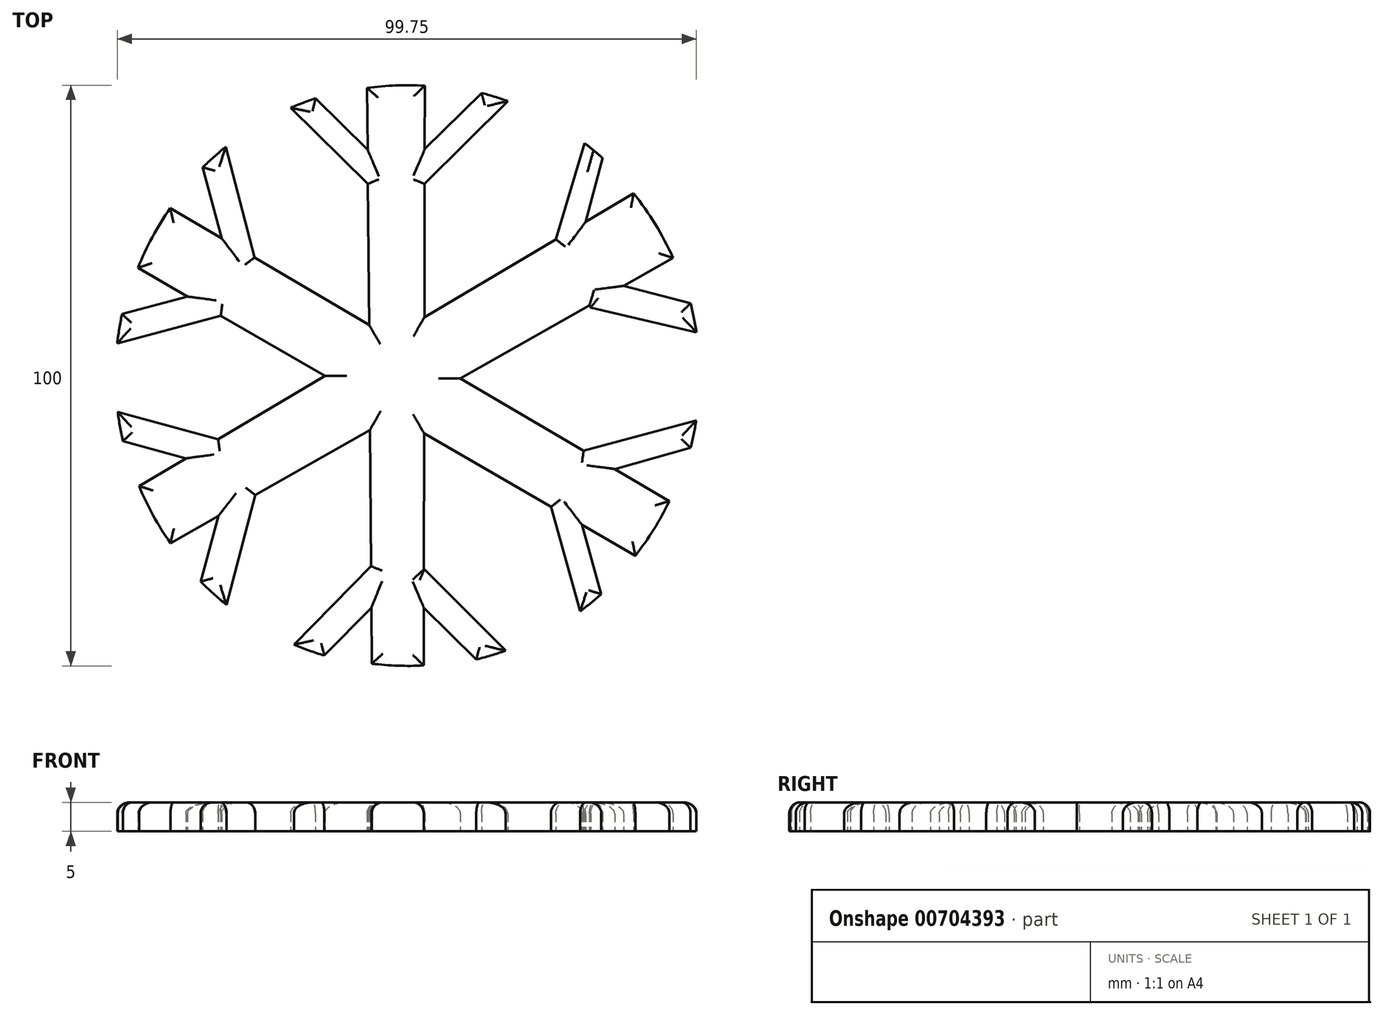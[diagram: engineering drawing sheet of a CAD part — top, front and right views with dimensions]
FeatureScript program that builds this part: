
annotation { "Feature Type Name" : "Feature", "Feature Type Description" : "" }
export const myFeature = defineFeature(function(context is Context, id is Id, definition is map)
    precondition{}
    {
        {
            var Q0;
            Q0=qCreatedBy(makeId("Top.planeOp"),FACE);
            var sketch = newSketch(context, id + "F0", { "sketchPlane" : qUnion([Q0])});
            skArc(sketch, "E0", {"start": v(-39.33, 28.82) * mm, "mid": v(-42.42, 23.84) * mm, "end": v(-44.9, 18.55) * mm});
            skPoint(sketch, "E1.center", {"position": v(0, 0) * mm});
            skLineSegment(sketch, "E2", {"start": v(-5.43, 49.51) * mm, "end": v(-4.63, -49.62) * mm});
            skLineSegment(sketch, "E3", {"start": v(-39.33, 28.82) * mm, "end": v(46.61, -21.62) * mm});
            skLineSegment(sketch, "E4", {"start": v(-44.7, -19.02) * mm, "end": v(40.46, 31.38) * mm});
            skLineSegment(sketch, "E5.MirrorCS", {"start": v(-39.3, -28.86) * mm, "end": v(47.24, 20.26) * mm});
            skLineSegment(sketch, "E6.MirrorCS", {"start": v(4.5, 49.91) * mm, "end": v(4.3, -49.92) * mm});
            skLineSegment(sketch, "E7.MirrorCS", {"start": v(-44.9, 18.55) * mm, "end": v(40.75, -31.02) * mm});
            skArc(sketch, "E8.trimOffspring", {"start": v(4.5, 49.91) * mm, "mid": v(-0.48, 49.96) * mm, "end": v(-5.43, 49.51) * mm});
            skArc(sketch, "E9.trimOffspring", {"start": v(-4.63, -49.62) * mm, "mid": v(-0.17, -49.97) * mm, "end": v(4.3, -49.92) * mm});
            skArc(sketch, "E10.trimOffspring", {"start": v(40.75, -31.02) * mm, "mid": v(43.94, -26.48) * mm, "end": v(46.61, -21.62) * mm});
            skArc(sketch, "E11.trimOffspring", {"start": v(47.24, 20.26) * mm, "mid": v(44.21, 26.04) * mm, "end": v(40.46, 31.38) * mm});
            skArc(sketch, "E12.trimOffspring", {"start": v(-44.7, -19.02) * mm, "mid": v(-42.28, -24.1) * mm, "end": v(-39.3, -28.86) * mm});
            skLineSegment(sketch, "E13", {"start": v(-24.84, 20.31) * mm, "end": v(-30.64, 10.3) * mm});
            skLineSegment(sketch, "E14", {"start": v(-24.84, 20.31) * mm, "end": v(-29.8, 39.35) * mm});
            skLineSegment(sketch, "E15", {"start": v(-30.64, 10.3) * mm, "end": v(-48.47, 5.54) * mm});
            skLineSegment(sketch, "E16", {"start": v(-48.47, 5.54) * mm, "end": v(-30.64, 10.3) * mm});
            skLineSegment(sketch, "E17", {"start": v(4.47, 33) * mm, "end": v(-5.3, 33) * mm});
            skLineSegment(sketch, "E18", {"start": v(4.47, 33) * mm, "end": v(18.77, 47.25) * mm});
            skLineSegment(sketch, "E19", {"start": v(-18.6, 46.1) * mm, "end": v(-5.3, 33) * mm});
            skArc(sketch, "E20", {"start": v(-29.8, 39.35) * mm, "mid": v(-31.82, 37.66) * mm, "end": v(-33.75, 35.86) * mm});
            skLineSegment(sketch, "E21.MirrorCS", {"start": v(-18.06, -46.33) * mm, "end": v(-4.77, -32.83) * mm});
            skLineSegment(sketch, "E22.MirrorCS", {"start": v(4.44, -33.37) * mm, "end": v(-4.77, -32.83) * mm});
            skLineSegment(sketch, "E23.MirrorCS", {"start": v(4.44, -33.37) * mm, "end": v(18.4, -47.39) * mm});
            skLineSegment(sketch, "E24.MirrorCS", {"start": v(31.78, -12.97) * mm, "end": v(51.24, -7.7) * mm});
            skLineSegment(sketch, "E25.MirrorCS", {"start": v(31.78, -12.97) * mm, "end": v(26.23, -22.61) * mm});
            skLineSegment(sketch, "E26.MirrorCS", {"start": v(31.24, -40.59) * mm, "end": v(26.23, -22.61) * mm});
            skLineSegment(sketch, "E27.MirrorCS", {"start": v(-24.7, -20.57) * mm, "end": v(-29.65, -39.47) * mm});
            skLineSegment(sketch, "E28.MirrorCS", {"start": v(-24.71, -20.64) * mm, "end": v(-30.29, -11) * mm});
            skLineSegment(sketch, "E29.MirrorCS", {"start": v(-48.38, -6.26) * mm, "end": v(-30.64, -11.09) * mm});
            skLineSegment(sketch, "E30.MirrorCS", {"start": v(33.06, 11.7) * mm, "end": v(27.08, 23.46) * mm});
            skLineSegment(sketch, "E31.MirrorCS", {"start": v(32, 40.02) * mm, "end": v(27.08, 23.46) * mm});
            skLineSegment(sketch, "E32.MirrorCS", {"start": v(33.06, 11.7) * mm, "end": v(51.28, 7.45) * mm});
            skLineSegment(sketch, "E33", {"start": v(-47.48, -11.31) * mm, "end": v(-36.66, -14.26) * mm});
            skLineSegment(sketch, "E34", {"start": v(-36.66, -14.26) * mm, "end": v(-31.04, -24.17) * mm});
            skLineSegment(sketch, "E35", {"start": v(-31.04, -24.17) * mm, "end": v(-34.12, -35.48) * mm});
            skLineSegment(sketch, "E36", {"start": v(-12.8, -48.22) * mm, "end": v(-4.71, -40) * mm});
            skLineSegment(sketch, "E37", {"start": v(-4.71, -40) * mm, "end": v(4.33, -40) * mm});
            skLineSegment(sketch, "E38", {"start": v(4.33, -40) * mm, "end": v(13.36, -48.89) * mm});
            skLineSegment(sketch, "E39", {"start": v(34.9, -37.64) * mm, "end": v(31.56, -25.7) * mm});
            skLineSegment(sketch, "E40", {"start": v(31.56, -25.7) * mm, "end": v(37.2, -16.1) * mm});
            skLineSegment(sketch, "E41", {"start": v(37.2, -16.1) * mm, "end": v(50.27, -12.44) * mm});
            skLineSegment(sketch, "E42", {"start": v(50.27, 12.44) * mm, "end": v(38.77, 15.45) * mm});
            skLineSegment(sketch, "E43", {"start": v(38.77, 15.45) * mm, "end": v(32.23, 26.5) * mm});
            skLineSegment(sketch, "E44", {"start": v(32.23, 26.5) * mm, "end": v(35.1, 37.46) * mm});
            skLineSegment(sketch, "E45", {"start": v(-14.33, 47.74) * mm, "end": v(-5.35, 38.9) * mm});
            skLineSegment(sketch, "E46", {"start": v(-5.35, 38.9) * mm, "end": v(4.48, 38.97) * mm});
            skLineSegment(sketch, "E47", {"start": v(4.48, 38.97) * mm, "end": v(14.27, 48.66) * mm});
            skLineSegment(sketch, "E48", {"start": v(-47.64, 10.6) * mm, "end": v(-36.36, 13.6) * mm});
            skLineSegment(sketch, "E49", {"start": v(-36.36, 13.6) * mm, "end": v(-30.48, 23.62) * mm});
            skLineSegment(sketch, "E50", {"start": v(-30.48, 23.62) * mm, "end": v(-33.75, 35.86) * mm});
            skArc(sketch, "E51.trimOffspring", {"start": v(-47.64, 10.6) * mm, "mid": v(-48.12, 8.07) * mm, "end": v(-48.47, 5.54) * mm});
            skArc(sketch, "E52.trimOffspring", {"start": v(-48.38, -6.26) * mm, "mid": v(-48, -8.8) * mm, "end": v(-47.48, -11.31) * mm});
            skArc(sketch, "E53.trimOffspring", {"start": v(-34.12, -35.48) * mm, "mid": v(-31.95, -37.54) * mm, "end": v(-29.65, -39.47) * mm});
            skArc(sketch, "E54.trimOffspring", {"start": v(-18.06, -46.33) * mm, "mid": v(-15.45, -47.35) * mm, "end": v(-12.8, -48.22) * mm});
            skArc(sketch, "E55.trimOffspring", {"start": v(13.36, -48.89) * mm, "mid": v(15.9, -48.2) * mm, "end": v(18.4, -47.39) * mm});
            skArc(sketch, "E56.trimOffspring", {"start": v(31.24, -40.59) * mm, "mid": v(33.1, -39.16) * mm, "end": v(34.9, -37.64) * mm});
            skArc(sketch, "E57.trimOffspring", {"start": v(50.27, -12.44) * mm, "mid": v(50.8, -10.09) * mm, "end": v(51.24, -7.7) * mm});
            skArc(sketch, "E58.trimOffspring", {"start": v(51.28, 7.45) * mm, "mid": v(50.84, 9.96) * mm, "end": v(50.27, 12.44) * mm});
            skArc(sketch, "E59.trimOffspring", {"start": v(35.1, 37.46) * mm, "mid": v(33.57, 38.77) * mm, "end": v(32, 40.02) * mm});
            skArc(sketch, "E60.trimOffspring", {"start": v(18.77, 47.25) * mm, "mid": v(16.54, 48.01) * mm, "end": v(14.27, 48.66) * mm});
            skArc(sketch, "E61.trimOffspring", {"start": v(-14.33, 47.74) * mm, "mid": v(-16.49, 46.96) * mm, "end": v(-18.6, 46.1) * mm});
            skSolve(sketch);
        }
        {
            var Q0;
            Q0 = qSketchRegion(id + "F0", true);
            var Q1;
            {var subQ5=sQuery(id+"F0.wireOp",EDGE,"E4");var subQ6=sQuery(id+"F0.wireOp",EDGE,"E2");var subQ7=makeQuery(id+"F0.imprint","INTERSECT",VERTEX,{"derivedFrom":[subQ6,subQ5]});Q1=makeQuery(id+"F0.imprint","IMPRINT",FACE,{"disambiguationData":[TD([[makeQuery(id+"F0.imprint","IMPRINT",EDGE,{"disambiguationData":[TD([[subQ7,-1.0]])],"derivedFrom":subQ6}),1.0]])]});}
            extrude(context, id + "F1", {"entities" : qUnion([Q0, Q1]), "depth" : 5 * mm, "offsetDistance" : 25 * mm});
        }
        {
            var Q0;
            Q0=makeQuery(id+"F1.opExtrude","CAP_FACE",FACE,{"disambiguationData":[OSD([sQuery(id+"F0.wireOp",EDGE,"E0"),sQuery(id+"F0.wireOp",EDGE,"E2"),sQuery(id+"F0.wireOp",EDGE,"E3"),sQuery(id+"F0.wireOp",EDGE,"E4"),sQuery(id+"F0.wireOp",EDGE,"E5.MirrorCS"),sQuery(id+"F0.wireOp",EDGE,"E6.MirrorCS"),sQuery(id+"F0.wireOp",EDGE,"E7.MirrorCS"),sQuery(id+"F0.wireOp",EDGE,"E8.trimOffspring"),sQuery(id+"F0.wireOp",EDGE,"E9.trimOffspring"),sQuery(id+"F0.wireOp",EDGE,"E10.trimOffspring"),sQuery(id+"F0.wireOp",EDGE,"E11.trimOffspring"),sQuery(id+"F0.wireOp",EDGE,"E12.trimOffspring"),sQuery(id+"F0.wireOp",EDGE,"E14"),sQuery(id+"F0.wireOp",EDGE,"E16"),sQuery(id+"F0.wireOp",EDGE,"E18"),sQuery(id+"F0.wireOp",EDGE,"E19"),sQuery(id+"F0.wireOp",EDGE,"E20"),sQuery(id+"F0.wireOp",EDGE,"E21.MirrorCS"),sQuery(id+"F0.wireOp",EDGE,"E22.MirrorCS"),sQuery(id+"F0.wireOp",EDGE,"E23.MirrorCS"),sQuery(id+"F0.wireOp",EDGE,"E24.MirrorCS"),sQuery(id+"F0.wireOp",EDGE,"E26.MirrorCS"),sQuery(id+"F0.wireOp",EDGE,"E27.MirrorCS"),sQuery(id+"F0.wireOp",EDGE,"E29.MirrorCS"),sQuery(id+"F0.wireOp",EDGE,"E30.MirrorCS"),sQuery(id+"F0.wireOp",EDGE,"E31.MirrorCS"),sQuery(id+"F0.wireOp",EDGE,"E32.MirrorCS"),sQuery(id+"F0.wireOp",EDGE,"E33"),sQuery(id+"F0.wireOp",EDGE,"E35"),sQuery(id+"F0.wireOp",EDGE,"E36"),sQuery(id+"F0.wireOp",EDGE,"E38"),sQuery(id+"F0.wireOp",EDGE,"E39"),sQuery(id+"F0.wireOp",EDGE,"E41"),sQuery(id+"F0.wireOp",EDGE,"E42"),sQuery(id+"F0.wireOp",EDGE,"E44"),sQuery(id+"F0.wireOp",EDGE,"E45"),sQuery(id+"F0.wireOp",EDGE,"E47"),sQuery(id+"F0.wireOp",EDGE,"E48"),sQuery(id+"F0.wireOp",EDGE,"E50"),sQuery(id+"F0.wireOp",EDGE,"E51.trimOffspring"),sQuery(id+"F0.wireOp",EDGE,"E52.trimOffspring"),sQuery(id+"F0.wireOp",EDGE,"E53.trimOffspring"),sQuery(id+"F0.wireOp",EDGE,"E54.trimOffspring"),sQuery(id+"F0.wireOp",EDGE,"E55.trimOffspring"),sQuery(id+"F0.wireOp",EDGE,"E56.trimOffspring"),sQuery(id+"F0.wireOp",EDGE,"E57.trimOffspring"),sQuery(id+"F0.wireOp",EDGE,"E58.trimOffspring"),sQuery(id+"F0.wireOp",EDGE,"E59.trimOffspring"),sQuery(id+"F0.wireOp",EDGE,"E60.trimOffspring"),sQuery(id+"F0.wireOp",EDGE,"E61.trimOffspring")])],"isStart":false});
            fillet(context, id + "F2", {"entities" : qUnion([Q0]), "radius" : 1.9 * mm, "tangentPropagation" : true, "allowEdgeOverflow" : false});
        }
    });
